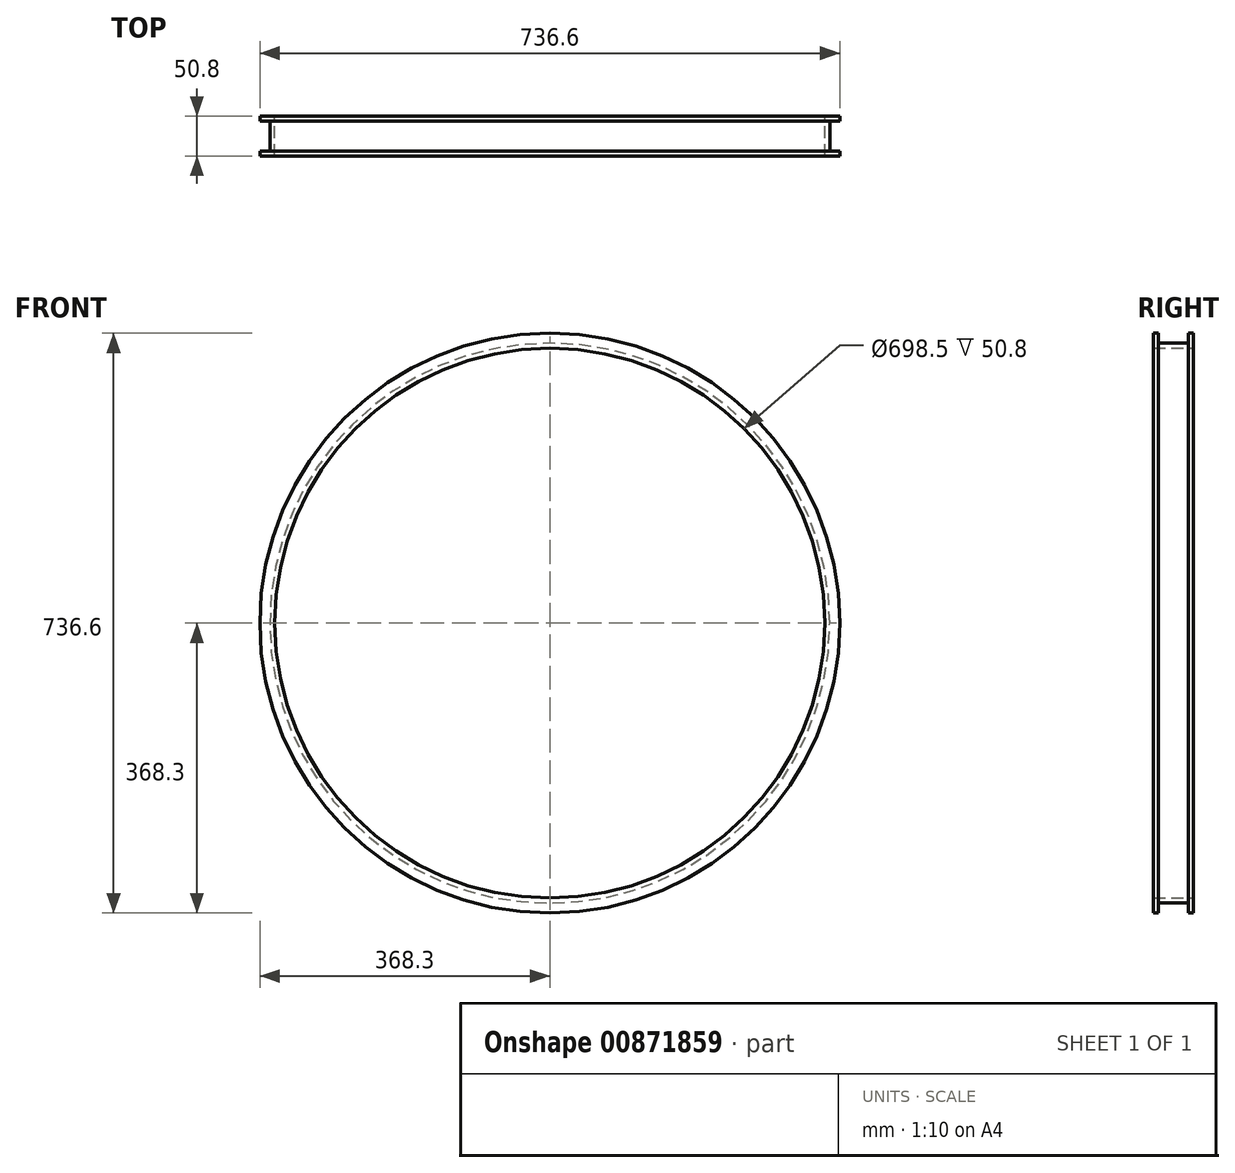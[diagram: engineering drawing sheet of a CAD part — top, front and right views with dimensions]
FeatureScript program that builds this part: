
annotation { "Feature Type Name" : "Feature", "Feature Type Description" : "" }
export const myFeature = defineFeature(function(context is Context, id is Id, definition is map)
    precondition{}
    {
        {
            var Q0;
            Q0=qCreatedBy(makeId("Front.planeOp"),FACE);
            var sketch = newSketch(context, id + "F0", { "sketchPlane" : qUnion([Q0])});
            skCircle(sketch, "E0", {"center": v(0, 0) * mm, "radius": 368.3 * mm});
            skSolve(sketch);
        }
        {
            var Q0;
            Q0=makeQuery(id+"F0.imprint","IMPRINT",FACE,{"disambiguationData":[TD([[makeQuery(id+"F0.imprint","IMPRINT",EDGE,{"derivedFrom":sQuery(id+"F0.wireOp",EDGE,"E0")}),1.0]])]});
            extrude(context, id + "F1", {"entities" : qUnion([Q0]), "depth" : 50.8 * mm, "offsetDistance" : 25.4 * mm});
        }
        {
            var Q0;
            Q0=sQuery(id+"F0.wireOp",VERTEX,"E0.center");
            var Q1;
            Q1=makeQuery(id+"F1.opExtrude","SWEPT_BODY",BODY,{"disambiguationData":[OSD([sQuery(id+"F0.wireOp",EDGE,"E0")])]});
            hole(context, id + "F2", {"style" : HoleStyle.SIMPLE, "endStyle" : HoleEndStyle.THROUGH, "oppositeDirection" : true, "holeDiameter" : 698.5 * mm, "majorDiameter" : 6.35 * mm, "isTappedThrough" : true, "tappedDepth" : 12.7 * mm, "tapClearance" : 3, "locations" : qUnion([Q0]), "scope" : qUnion([Q1])});
        }
        {
            var Q0;
            Q0=makeQuery(id+"F1.opExtrude","SWEPT_FACE",FACE,{"disambiguationData":[OSD([sQuery(id+"F0.wireOp",EDGE,"E0")])]});
            shell(context, id + "F3", {"entities" : qUnion([Q0]), "thickness" : 6.35 * mm});
        }
    });
